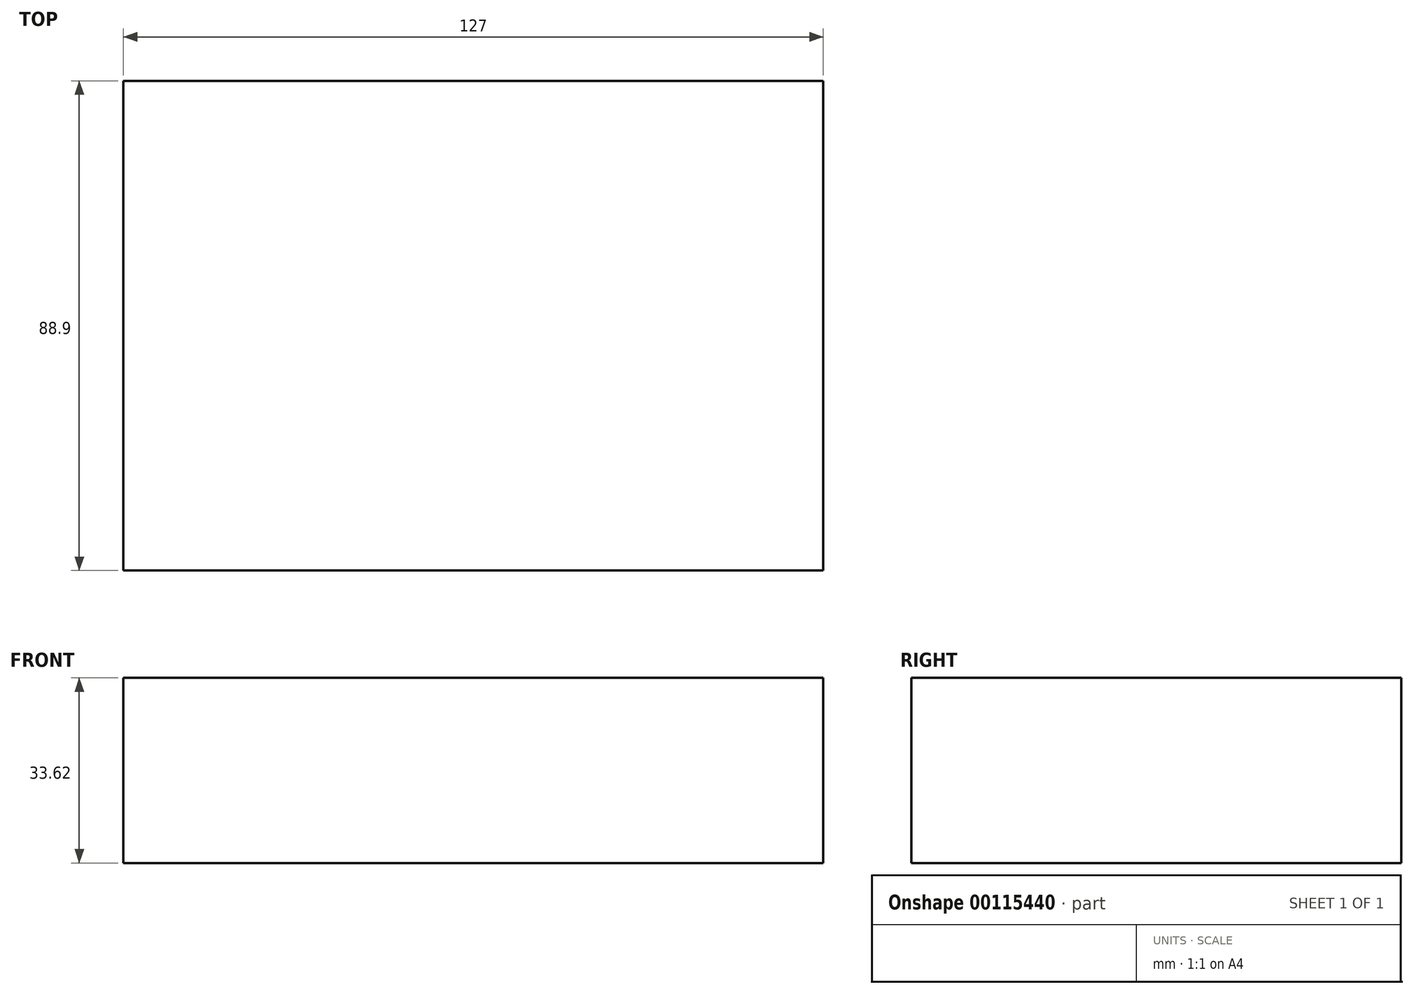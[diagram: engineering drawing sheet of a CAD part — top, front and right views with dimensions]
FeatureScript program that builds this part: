
annotation { "Feature Type Name" : "Feature", "Feature Type Description" : "" }
export const myFeature = defineFeature(function(context is Context, id is Id, definition is map)
    precondition{}
    {
        {
            var Q0;
            Q0=qCreatedBy(makeId("Top.planeOp"),FACE);
            var sketch = newSketch(context, id + "F0", { "sketchPlane" : qUnion([Q0])});
            skLineSegment(sketch, "E0.bottom", {"start": v(-64.43, 47.37) * mm, "end": v(62.57, 47.37) * mm});
            skLineSegment(sketch, "E0.top", {"start": v(-64.43, -41.53) * mm, "end": v(62.57, -41.53) * mm});
            skLineSegment(sketch, "E0.left", {"start": v(-64.43, 47.37) * mm, "end": v(-64.43, -41.53) * mm});
            skLineSegment(sketch, "E0.right", {"start": v(62.57, 47.37) * mm, "end": v(62.57, -41.53) * mm});
            skSolve(sketch);
        }
        {
            var Q0;
            Q0 = qSketchRegion(id + "F0", true);
            extrude(context, id + "F1", {"entities" : qUnion([Q0]), "depth" : 33.62 * mm});
        }
    });
